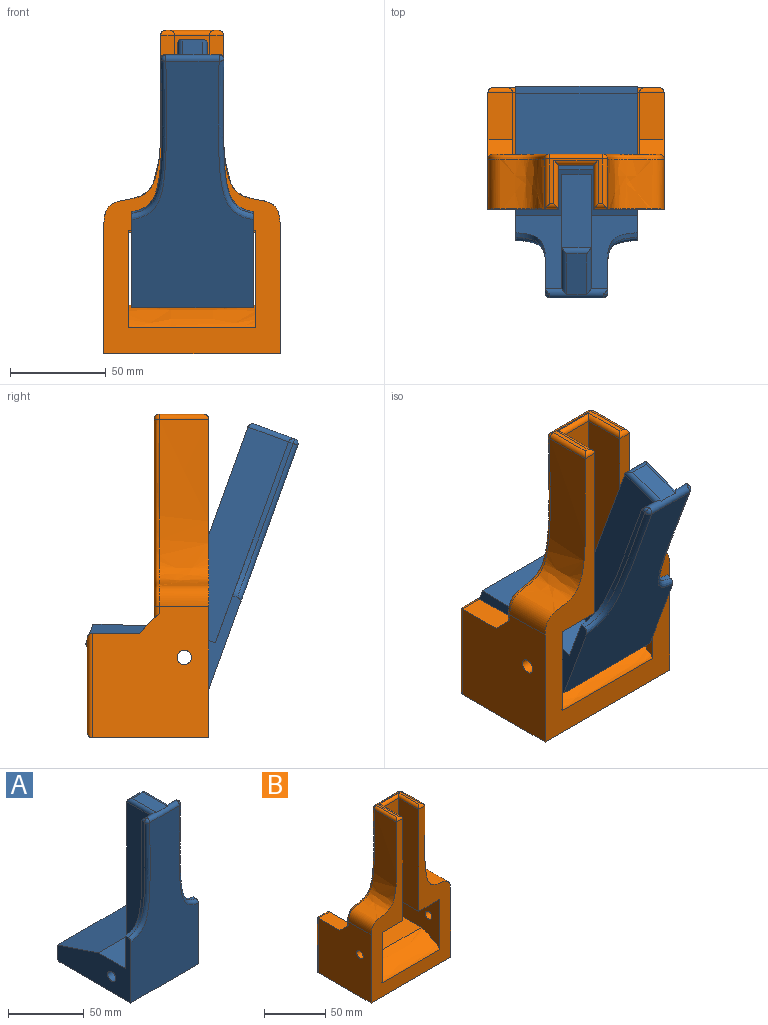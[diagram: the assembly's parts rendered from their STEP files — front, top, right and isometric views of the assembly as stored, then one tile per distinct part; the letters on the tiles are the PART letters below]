
ASSEMBLY  parts=2 mates=1
PART A: 27 faces, bbox 68x68.8x139.9 mm
  f0: plane 68.77x51.87mm, normal (-1,0,0), area 1586mm2, adj f2,f3,f4,f6,f9,f10,f12,f15
  f1: plane 22.69x10.16mm, normal (0,0,1), area 230.6mm2, adj f16,f17,f18,f21
  f2: plane 113.89x26.28mm, normal (0,1,0), area 1457.9mm2, adj f0,f8,f9,f15,f21,f23
  f3: plane 137.17x63.52mm, normal (0,-1,0), area 5751mm2, adj f0,f5,f6,f20,f21,f25
  f4: plane 63.5x10.16mm, normal (0,1,0), area 645.2mm2, adj f0,f5,f12,f26
  f5: plane 68.77x51.86mm, normal (1,0,0), area 1586mm2, adj f3,f4,f6,f9,f10,f12,f13,f14
  f6: plane 66.04x63.5mm, normal (0,0,-1), area 4193.5mm2, adj f0,f3,f5,f26
  f7: plane 111.76x22.69mm, normal (1,0,0), area 2536.1mm2, adj f9,f11,f13,f18
  f8: plane 111.76x22.69mm, normal (-1,0,0), area 2536.1mm2, adj f2,f9,f11,f17
  f9: plane 63.5x25.4mm, normal (0,0,1), area 1267.1mm2, adj f0,f2,f5,f7,f8,f11,f12,f13
  f10: cylinder r=3.77mm len=63.5mm, axis (-1,0,0), area 1504.9mm2, adj f0,f5
  f11: plane 111.76x15.24mm, normal (0,1,0), area 1703.2mm2, adj f7,f8,f9,f16
  f12: plane 63.5x38.1mm, normal (0,0.32,0.95), area 2550.2mm2, adj f0,f4,f5,f9
  f13: plane 113.89x26.28mm, normal (0,1,0), area 1457.9mm2, adj f5,f7,f9,f14,f19,f21
  f14: extruded ~85.46x15.76mm, area 235.2mm2, adj f5,f13,f19,f20
  f15: extruded ~85.46x15.76mm, area 235.2mm2, adj f0,f2,f23,f25
  f16: cylinder r=2.54mm len=15.24mm, axis (-1,0,0), area 50.7mm2, adj f1,f11,f17,f18
  f17: cylinder r=2.54mm len=25.23mm, axis (0,1,0), area 90.5mm2, adj f1,f8,f16,f21
  f18: cylinder r=2.54mm len=25.23mm, axis (0,-1,0), area 90.5mm2, adj f1,f7,f16,f21
  f19: cylinder r=2.54mm len=2.56mm, axis (0,-1,0), area 6.5mm2, adj f13,f14,f21,f22
  f20: bspline ~89.96x19.29mm, area 375.5mm2, adj f3,f5,f14,f22
  f21: cylinder r=2.54mm len=32.83mm, axis (1,0,0), area 180.9mm2, adj f1,f2,f3,f13,f17,f18,f19,f22
  f22: sphere r=2.54mm, area 10.2mm2, adj f19,f20,f21
  f23: cylinder r=2.54mm len=2.56mm, axis (0,-1,0), area 6.5mm2, adj f2,f15,f21,f24
  f24: sphere r=2.54mm, area 13.6mm2, adj f21,f23,f25
  f25: bspline ~89.96x19.29mm, area 375.5mm2, adj f0,f3,f15,f24
  f26: cylinder r=2.54mm len=63.5mm, axis (-1,0,0), area 253.4mm2, adj f0,f4,f5,f6
PART B: 47 faces, bbox 91.9x63.5x169.8 mm
  f0: plane 68.43x60.96mm, normal (1,0,0), area 3695.7mm2, adj f3,f9,f11,f17,f21,f23,f26,f41
  f1: plane 27.75x23.48mm, normal (0,0,1), area 117.6mm2, adj f25,f27,f28,f30,f31,f33,f34,f35
  f2: plane 68.43x60.96mm, normal (-1,0,0), area 3695.7mm2, adj f3,f9,f12,f18,f22,f24,f38,f45
  f3: plane 168.5x91.95mm, normal (0,-1,0), area 5101.4mm2, adj f0,f2,f6,f7,f9,f10,f13,f14
  f4: plane 104.17x86.87mm, normal (0,1,0), area 3914.4mm2, adj f6,f7,f20,f21,f22,f26,f29,f34
  f5: plane 86.87x49.53mm, normal (0,1,0), area 2210.3mm2, adj f39,f40,f41,f42,f43,f44,f45,f46
  f6: plane 60.96x50.38mm, normal (1,0,0), area 2122.8mm2, adj f3,f4,f8,f10,f12,f13,f18,f19
  f7: plane 60.96x50.38mm, normal (-1,0,0), area 2122.8mm2, adj f3,f4,f8,f10,f11,f15,f17,f19
  f8: plane 66.55x39.67mm, normal (0,0,1), area 2639.9mm2, adj f6,f7,f10,f42
  f9: plane 91.95x60.96mm, normal (0,0,-1), area 5605.2mm2, adj f0,f2,f3,f43
  f10: extruded ~66.55x21.29mm, area 1652.1mm2, adj f3,f6,f7,f8
  f11: cylinder r=3.77mm len=12.7mm, axis (-1,0,0), area 301mm2, adj f0,f7
  f12: cylinder r=3.77mm len=12.7mm, axis (1,0,0), area 301mm2, adj f2,f6
  f13: plane 24.13x22.86mm, normal (0,0,-1), area 551.6mm2, adj f3,f6,f14,f19
  f14: plane 102.18x22.86mm, normal (1,0,0), area 2335.8mm2, adj f3,f13,f19,f31
  f15: plane 24.13x22.86mm, normal (0,0,-1), area 551.6mm2, adj f3,f7,f16,f19
  f16: plane 102.18x22.86mm, normal (-1,0,0), area 2335.8mm2, adj f3,f15,f19,f25
  f17: plane 24.78x12.7mm, normal (0,0,1), area 314.7mm2, adj f0,f7,f21,f39
  f18: plane 24.78x12.7mm, normal (0,0,1), area 314.7mm2, adj f2,f6,f22,f46
  f19: plane 103.03x66.55mm, normal (0,-1,0), area 1925.1mm2, adj f6,f7,f13,f14,f15,f16,f20,f28
  f20: plane 66.55x5.7mm, normal (0,0,-1), area 379.6mm2, adj f4,f6,f7,f19
  f21: plane 12.7x10.16mm, normal (0,0.71,0.71), area 138.8mm2, adj f0,f4,f7,f17,f26
  f22: plane 12.7x10.16mm, normal (0,0.71,0.71), area 138.8mm2, adj f2,f4,f6,f18,f38
  f23: extruded ~97.91x29.98mm, area 2968.9mm2, adj f0,f3,f29,f30
  f24: extruded ~97.91x29.98mm, area 2968.9mm2, adj f2,f3,f35,f37
  f25: cylinder r=2.54mm len=25.4mm, axis (0,-1,0), area 91.2mm2, adj f1,f16,f27,f28
  f26: cylinder r=2.54mm len=6.2mm, axis (0,0,1), area 21.1mm2, adj f0,f4,f21,f29
  f27: cylinder r=2.54mm len=7.27mm, axis (1,0,0), area 21.7mm2, adj f1,f3,f25,f30
  f28: cylinder r=2.54mm len=23.37mm, axis (-1,0,0), area 80.3mm2, adj f1,f19,f25,f31
  f29: bspline ~111.8x32.53mm, area 455.3mm2, adj f4,f23,f26,f32
  f30: cylinder r=2.54mm len=26.02mm, axis (0,-1,0), area 100.7mm2, adj f1,f3,f23,f27,f32
  f31: cylinder r=2.54mm len=25.4mm, axis (0,1,0), area 91.2mm2, adj f1,f14,f28,f33
  f32: sphere r=2.54mm, area 10.2mm2, adj f29,f30,f34
  f33: cylinder r=2.54mm len=7.27mm, axis (-1,0,0), area 21.7mm2, adj f1,f3,f31,f35
  f34: cylinder r=2.54mm len=27.75mm, axis (1,0,0), area 110.7mm2, adj f1,f4,f32,f36
  f35: cylinder r=2.54mm len=26.02mm, axis (0,-1,0), area 100.7mm2, adj f1,f3,f24,f33,f36
  f36: sphere r=2.54mm, area 10.2mm2, adj f34,f35,f37
  f37: bspline ~111.8x32.53mm, area 455.3mm2, adj f4,f24,f36,f38
  f38: cylinder r=2.54mm len=6.2mm, axis (0,0,-1), area 21.1mm2, adj f2,f4,f22,f37
  f39: cylinder r=2.54mm len=12.7mm, axis (1,0,0), area 43.3mm2, adj f5,f17,f40,f41
  f40: cylinder r=2.54mm len=31.75mm, axis (0,0,-1), area 116.5mm2, adj f5,f7,f39,f42
  f41: cylinder r=2.54mm len=54.61mm, axis (0,0,1), area 210.5mm2, adj f0,f5,f39,f43
  f42: cylinder r=2.54mm len=71.63mm, axis (1,0,0), area 272.9mm2, adj f5,f8,f40,f44
  f43: cylinder r=2.54mm len=91.95mm, axis (-1,0,0), area 359.5mm2, adj f5,f9,f41,f45
  f44: cylinder r=2.54mm len=31.75mm, axis (0,0,1), area 116.5mm2, adj f5,f6,f42,f46
  f45: cylinder r=2.54mm len=54.61mm, axis (0,0,-1), area 210.5mm2, adj f2,f5,f43,f46
  f46: cylinder r=2.54mm len=12.7mm, axis (1,0,0), area 43.3mm2, adj f5,f18,f44,f45
PLACE A rot(axis=(1,0,0),20deg) t=(-20.27,105.59,-11.27)mm
PLACE B rot(axis=(-0.41,-0.29,-0.87),0deg) t=(-20.53,100.48,-7.7)mm
MATE revolute B.f11 <-> A.f10  axis (1,0,0) through (57.2,113.18,5)mm
